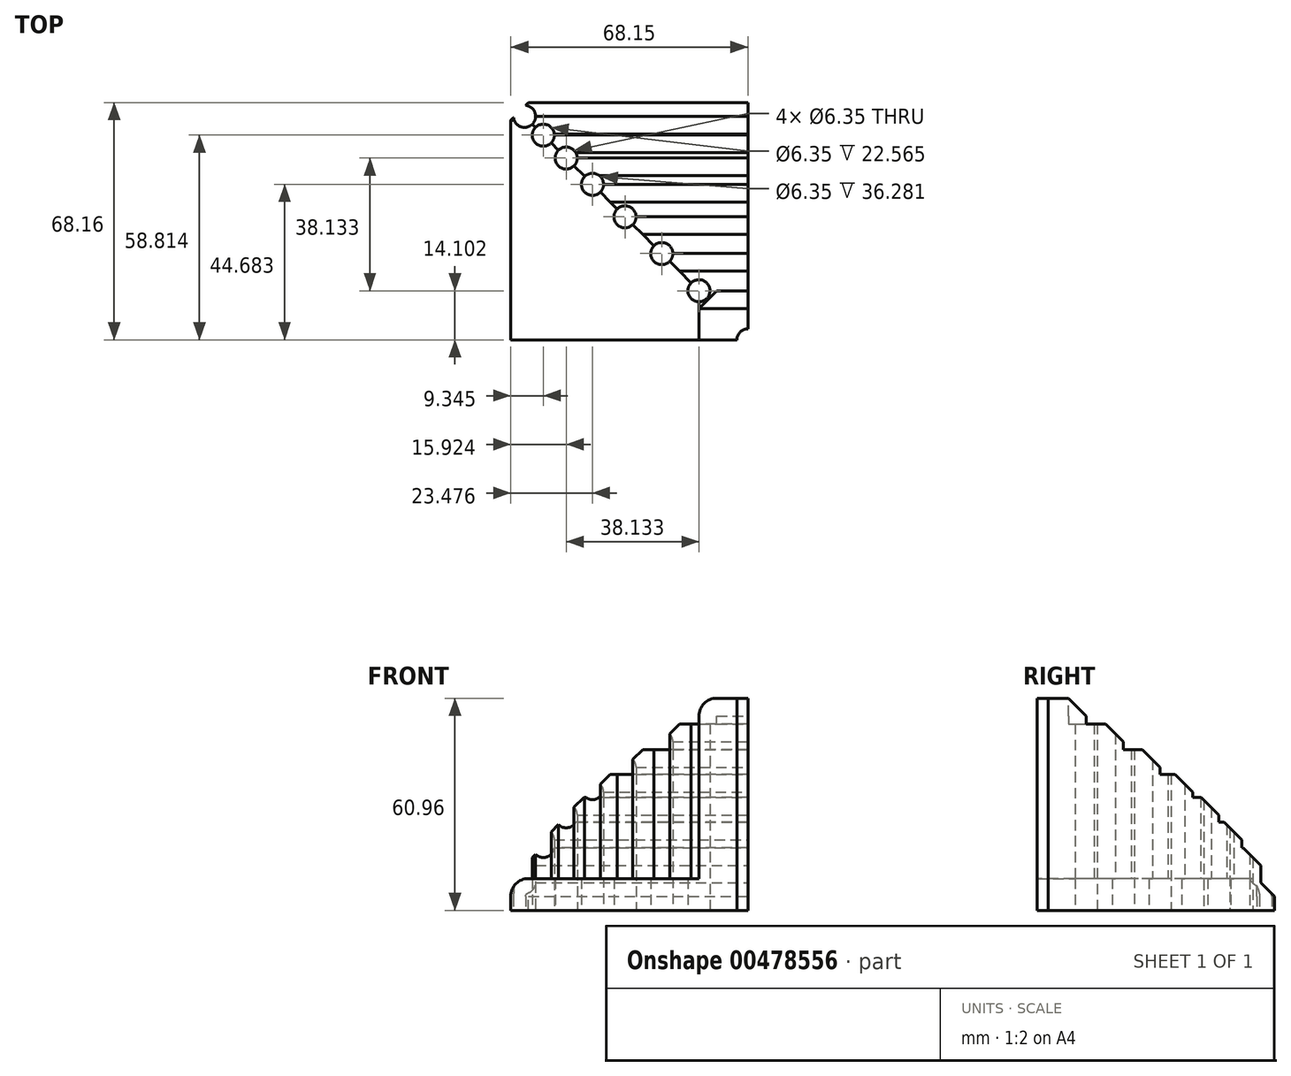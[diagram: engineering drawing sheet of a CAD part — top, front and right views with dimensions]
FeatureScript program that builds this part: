
annotation { "Feature Type Name" : "Feature", "Feature Type Description" : "" }
export const myFeature = defineFeature(function(context is Context, id is Id, definition is map)
    precondition{}
    {
        {
            var Q0;
            Q0=qCreatedBy(makeId("Top.planeOp"),FACE);
            var sketch = newSketch(context, id + "F0", { "sketchPlane" : qUnion([Q0])});
            skLineSegment(sketch, "E0.bottom", {"start": v(-29.57, 37.12) * mm, "end": v(38.58, 37.12) * mm});
            skLineSegment(sketch, "E0.top", {"start": v(-29.57, -31.04) * mm, "end": v(38.58, -31.04) * mm});
            skLineSegment(sketch, "E0.left", {"start": v(-29.57, 37.12) * mm, "end": v(-29.57, -31.04) * mm});
            skLineSegment(sketch, "E0.right", {"start": v(38.58, 37.12) * mm, "end": v(38.58, -31.04) * mm});
            skLineSegment(sketch, "E1.top", {"start": v(-27.22, -31.04) * mm, "end": v(38.58, -31.04) * mm});
            skLineSegment(sketch, "E1.right", {"start": v(38.58, 33.6) * mm, "end": v(38.58, -31.04) * mm});
            skLineSegment(sketch, "E2", {"start": v(-29.57, 37.12) * mm, "end": v(24.49, -16.94) * mm});
            skLineSegment(sketch, "E3.bottom", {"start": v(-25.63, 33.18) * mm, "end": v(38.58, 33.18) * mm});
            skLineSegment(sketch, "E3.top", {"start": v(-25.63, -31.04) * mm, "end": v(38.58, -31.04) * mm});
            skLineSegment(sketch, "E3.left", {"start": v(-25.63, 33.18) * mm, "end": v(-25.63, -31.04) * mm});
            skLineSegment(sketch, "E3.right", {"start": v(38.58, 33.18) * mm, "end": v(38.58, -31.04) * mm});
            skLineSegment(sketch, "E4.bottom", {"start": v(-20.22, 27.77) * mm, "end": v(38.58, 27.77) * mm});
            skLineSegment(sketch, "E4.top", {"start": v(-20.22, -31.04) * mm, "end": v(38.58, -31.04) * mm});
            skLineSegment(sketch, "E4.left", {"start": v(-20.22, 27.77) * mm, "end": v(-20.22, -31.04) * mm});
            skLineSegment(sketch, "E4.right", {"start": v(38.58, 27.77) * mm, "end": v(38.58, -31.04) * mm});
            skLineSegment(sketch, "E5.bottom", {"start": v(-13.65, 21.2) * mm, "end": v(38.58, 21.2) * mm});
            skLineSegment(sketch, "E5.top", {"start": v(-13.65, -31.04) * mm, "end": v(38.58, -31.04) * mm});
            skLineSegment(sketch, "E5.left", {"start": v(-13.65, 21.2) * mm, "end": v(-13.65, -31.04) * mm});
            skLineSegment(sketch, "E5.right", {"start": v(38.58, 21.2) * mm, "end": v(38.58, -31.04) * mm});
            skLineSegment(sketch, "E6.bottom", {"start": v(-6.1, 13.64) * mm, "end": v(38.58, 13.64) * mm});
            skLineSegment(sketch, "E6.top", {"start": v(-6.1, -31.04) * mm, "end": v(38.58, -31.04) * mm});
            skLineSegment(sketch, "E6.left", {"start": v(-6.1, 13.64) * mm, "end": v(-6.1, -31.04) * mm});
            skLineSegment(sketch, "E6.right", {"start": v(38.58, 13.64) * mm, "end": v(38.58, -31.04) * mm});
            skLineSegment(sketch, "E7.bottom", {"start": v(3.25, 4.3) * mm, "end": v(38.58, 4.3) * mm});
            skLineSegment(sketch, "E7.top", {"start": v(3.25, -31.04) * mm, "end": v(38.58, -31.04) * mm});
            skLineSegment(sketch, "E7.left", {"start": v(3.25, 4.3) * mm, "end": v(3.25, -31.04) * mm});
            skLineSegment(sketch, "E7.right", {"start": v(38.58, 4.3) * mm, "end": v(38.58, -31.04) * mm});
            skLineSegment(sketch, "E8.bottom", {"start": v(13.81, -6.26) * mm, "end": v(38.58, -6.26) * mm});
            skLineSegment(sketch, "E8.top", {"start": v(13.81, -31.04) * mm, "end": v(38.58, -31.04) * mm});
            skLineSegment(sketch, "E8.left", {"start": v(13.81, -6.26) * mm, "end": v(13.81, -31.04) * mm});
            skLineSegment(sketch, "E8.right", {"start": v(38.58, -6.26) * mm, "end": v(38.58, -31.04) * mm});
            skLineSegment(sketch, "E9.bottom", {"start": v(24.49, -16.94) * mm, "end": v(38.58, -16.94) * mm});
            skLineSegment(sketch, "E9.top", {"start": v(24.49, -31.04) * mm, "end": v(38.58, -31.04) * mm});
            skLineSegment(sketch, "E9.left", {"start": v(24.49, -16.94) * mm, "end": v(24.49, -31.04) * mm});
            skLineSegment(sketch, "E9.right", {"start": v(38.58, -16.94) * mm, "end": v(38.58, -31.04) * mm});
            skSolve(sketch);
        }
        {
            var Q0;
            {var subQ1=sQuery(id+"F0.wireOp",EDGE,"E0.bottom");Q0=makeQuery(id+"F0.imprint","IMPRINT",FACE,{"disambiguationData":[TD([[makeQuery(id+"F0.imprint","IMPRINT",EDGE,{"derivedFrom":subQ1}),-1.0]])]});}
            var Q1;
            Q1=makeQuery(id+"F0.imprint","IMPRINT",FACE,{"disambiguationData":[TD([[makeQuery(id+"F0.imprint","IMPRINT",EDGE,{"derivedFrom":sQuery(id+"F0.wireOp",EDGE,"E0.top")}),1.0]])]});
            extrude(context, id + "F1", {"entities" : qUnion([Q0, Q1]), "depth" : 9.14 * mm});
        }
        {
            var Q0;
            Q0=makeQuery(id+"F0.imprint","IMPRINT",FACE,{"disambiguationData":[TD([[makeQuery(id+"F0.imprint","IMPRINT",EDGE,{"derivedFrom":sQuery(id+"F0.wireOp",EDGE,"E3.top")}),1.0]])]});
            var Q1;
            {var subQ0=sQuery(id+"F0.wireOp",EDGE,"E3.bottom");Q1=makeQuery(id+"F0.imprint","IMPRINT",FACE,{"disambiguationData":[TD([[makeQuery(id+"F0.imprint","IMPRINT",EDGE,{"derivedFrom":subQ0}),-1.0]])]});}
            extrude(context, id + "F2", {"entities" : qUnion([Q0, Q1]), "operationType" : NewBodyOperationType.ADD, "depth" : 18.03 * mm});
        }
        {
            var Q0;
            Q0=makeQuery(id+"F0.imprint","IMPRINT",FACE,{"disambiguationData":[TD([[makeQuery(id+"F0.imprint","IMPRINT",EDGE,{"derivedFrom":sQuery(id+"F0.wireOp",EDGE,"E4.top")}),1.0]])]});
            var Q1;
            {var subQ0=sQuery(id+"F0.wireOp",EDGE,"E4.bottom");Q1=makeQuery(id+"F0.imprint","IMPRINT",FACE,{"disambiguationData":[TD([[makeQuery(id+"F0.imprint","IMPRINT",EDGE,{"derivedFrom":subQ0}),-1.0]])]});}
            extrude(context, id + "F3", {"entities" : qUnion([Q0, Q1]), "operationType" : NewBodyOperationType.ADD, "depth" : 25.4 * mm});
        }
        {
            var Q0;
            {var subQ0=sQuery(id+"F0.wireOp",EDGE,"E5.bottom");Q0=makeQuery(id+"F0.imprint","IMPRINT",FACE,{"disambiguationData":[TD([[makeQuery(id+"F0.imprint","IMPRINT",EDGE,{"derivedFrom":subQ0}),-1.0]])]});}
            var Q1;
            Q1=makeQuery(id+"F0.imprint","IMPRINT",FACE,{"disambiguationData":[TD([[makeQuery(id+"F0.imprint","IMPRINT",EDGE,{"derivedFrom":sQuery(id+"F0.wireOp",EDGE,"E5.top")}),1.0]])]});
            extrude(context, id + "F4", {"entities" : qUnion([Q0, Q1]), "operationType" : NewBodyOperationType.ADD, "depth" : 32.5 * mm});
        }
        {
            var Q0;
            Q0=makeQuery(id+"F0.imprint","IMPRINT",FACE,{"disambiguationData":[TD([[makeQuery(id+"F0.imprint","IMPRINT",EDGE,{"derivedFrom":sQuery(id+"F0.wireOp",EDGE,"E6.top")}),1.0]])]});
            var Q1;
            {var subQ0=sQuery(id+"F0.wireOp",EDGE,"E6.bottom");Q1=makeQuery(id+"F0.imprint","IMPRINT",FACE,{"disambiguationData":[TD([[makeQuery(id+"F0.imprint","IMPRINT",EDGE,{"derivedFrom":subQ0}),-1.0]])]});}
            extrude(context, id + "F5", {"entities" : qUnion([Q0, Q1]), "operationType" : NewBodyOperationType.ADD, "depth" : 39.12 * mm});
        }
        {
            var Q0;
            Q0=makeQuery(id+"F0.imprint","IMPRINT",FACE,{"disambiguationData":[TD([[makeQuery(id+"F0.imprint","IMPRINT",EDGE,{"derivedFrom":sQuery(id+"F0.wireOp",EDGE,"E7.top")}),1.0]])]});
            var Q1;
            {var subQ0=sQuery(id+"F0.wireOp",EDGE,"E7.bottom");Q1=makeQuery(id+"F0.imprint","IMPRINT",FACE,{"disambiguationData":[TD([[makeQuery(id+"F0.imprint","IMPRINT",EDGE,{"derivedFrom":subQ0}),-1.0]])]});}
            extrude(context, id + "F6", {"entities" : qUnion([Q0, Q1]), "operationType" : NewBodyOperationType.ADD, "depth" : 46.23 * mm});
        }
        {
            var Q0;
            {var subQ2=sQuery(id+"F0.wireOp",EDGE,"E8.bottom");Q0=makeQuery(id+"F0.imprint","IMPRINT",FACE,{"disambiguationData":[TD([[makeQuery(id+"F0.imprint","IMPRINT",EDGE,{"derivedFrom":subQ2}),-1.0]])]});}
            var Q1;
            Q1=makeQuery(id+"F0.imprint","IMPRINT",FACE,{"disambiguationData":[TD([[makeQuery(id+"F0.imprint","IMPRINT",EDGE,{"derivedFrom":sQuery(id+"F0.wireOp",EDGE,"E8.top")}),1.0]])]});
            extrude(context, id + "F7", {"entities" : qUnion([Q0, Q1]), "operationType" : NewBodyOperationType.ADD, "depth" : 53.6 * mm});
        }
        {
            var Q0;
            Q0=makeQuery(id+"F0.imprint","IMPRINT",FACE,{"disambiguationData":[TD([[makeQuery(id+"F0.imprint","IMPRINT",EDGE,{"derivedFrom":sQuery(id+"F0.wireOp",EDGE,"E9.bottom")}),-1.0]])]});
            extrude(context, id + "F8", {"entities" : qUnion([Q0]), "operationType" : NewBodyOperationType.ADD, "depth" : 60.96 * mm});
        }
        {
            var Q0;
            Q0=makeQuery(id+"F1.opExtrude","CAP_EDGE",EDGE,{"disambiguationData":[OSD([sQuery(id+"F0.wireOp",EDGE,"E0.left")])],"isStart":false});
            var Q1;
            Q1=makeQuery(id+"F2.opExtrude","CAP_EDGE",EDGE,{"disambiguationData":[OSD([sQuery(id+"F0.wireOp",EDGE,"E3.left")])],"isStart":false});
            var Q2;
            Q2=makeQuery(id+"F3.opExtrude","CAP_EDGE",EDGE,{"disambiguationData":[OSD([sQuery(id+"F0.wireOp",EDGE,"E4.left")])],"isStart":false});
            var Q3;
            Q3=makeQuery(id+"F4.opExtrude","CAP_EDGE",EDGE,{"disambiguationData":[OSD([sQuery(id+"F0.wireOp",EDGE,"E5.left")])],"isStart":false});
            var Q4;
            Q4=makeQuery(id+"F5.opExtrude","CAP_EDGE",EDGE,{"disambiguationData":[OSD([sQuery(id+"F0.wireOp",EDGE,"E6.left")])],"isStart":false});
            var Q5;
            Q5=makeQuery(id+"F6.opExtrude","CAP_EDGE",EDGE,{"disambiguationData":[OSD([sQuery(id+"F0.wireOp",EDGE,"E7.left")])],"isStart":false});
            var Q6;
            Q6=makeQuery(id+"F7.opExtrude","CAP_EDGE",EDGE,{"disambiguationData":[OSD([sQuery(id+"F0.wireOp",EDGE,"E8.left")])],"isStart":false});
            var Q7;
            Q7=makeQuery(id+"F8.opExtrude","CAP_EDGE",EDGE,{"disambiguationData":[OSD([sQuery(id+"F0.wireOp",EDGE,"E9.left")])],"isStart":false});
            fillet(context, id + "F9", {"entities" : qUnion([Q0, Q1, Q2, Q3, Q4, Q5, Q6, Q7]), "radius" : 5.08 * mm, "tangentPropagation" : true, "allowEdgeOverflow" : false});
        }
        {
            var Q0;
            Q0=makeQuery(id+"F3.opExtrude","CAP_EDGE",EDGE,{"disambiguationData":[OSD([sQuery(id+"F0.wireOp",EDGE,"E4.bottom")])],"isStart":false});
            var Q1;
            Q1=makeQuery(id+"F4.opExtrude","CAP_EDGE",EDGE,{"disambiguationData":[OSD([sQuery(id+"F0.wireOp",EDGE,"E5.bottom")])],"isStart":false});
            var Q2;
            Q2=makeQuery(id+"F5.opExtrude","CAP_EDGE",EDGE,{"disambiguationData":[OSD([sQuery(id+"F0.wireOp",EDGE,"E6.bottom")])],"isStart":false});
            var Q3;
            Q3=makeQuery(id+"F6.opExtrude","CAP_EDGE",EDGE,{"disambiguationData":[OSD([sQuery(id+"F0.wireOp",EDGE,"E7.bottom")])],"isStart":false});
            var Q4;
            Q4=makeQuery(id+"F7.opExtrude","CAP_EDGE",EDGE,{"disambiguationData":[OSD([sQuery(id+"F0.wireOp",EDGE,"E8.bottom")])],"isStart":false});
            var Q5;
            Q5=makeQuery(id+"F8.opExtrude","CAP_EDGE",EDGE,{"disambiguationData":[OSD([sQuery(id+"F0.wireOp",EDGE,"E9.bottom")])],"isStart":false});
            var Q6;
            Q6=makeQuery(id+"F2.opExtrude","CAP_EDGE",EDGE,{"disambiguationData":[OSD([sQuery(id+"F0.wireOp",EDGE,"E3.bottom")])],"isStart":false});
            chamfer(context, id + "F10", {"entities" : qUnion([Q0, Q1, Q2, Q3, Q4, Q5, Q6]), "width" : 5.08 * mm, "tangentPropagation" : true});
        }
        {
            var Q0;
            Q0=makeQuery(id+"F1.opExtrude","CAP_EDGE",EDGE,{"disambiguationData":[OSD([sQuery(id+"F0.wireOp",EDGE,"E0.bottom")])],"isStart":false});
            chamfer(context, id + "F11", {"entities" : qUnion([Q0]), "width" : 5.08 * mm, "tangentPropagation" : true});
        }
        {
            var Q0;
            Q0=sQuery(id+"F0.wireOp",VERTEX,"E0.bottom.start");
            var Q1;
            Q1=sQuery(id+"F0.wireOp",VERTEX,"E7.left.start");
            var Q2;
            Q2=sQuery(id+"F0.wireOp",VERTEX,"E5.left.start");
            var Q3;
            Q3=sQuery(id+"F0.wireOp",VERTEX,"E3.left.start");
            var Q4;
            Q4=sQuery(id+"F0.wireOp",VERTEX,"E4.bottom.start");
            var Q5;
            Q5=sQuery(id+"F0.wireOp",VERTEX,"E6.bottom.start");
            var Q6;
            Q6=sQuery(id+"F0.wireOp",VERTEX,"E9.left.start");
            var Q7;
            Q7=sQuery(id+"F0.wireOp",VERTEX,"E8.bottom.start");
            var Q8;
            Q8=sQuery(id+"F0.wireOp",VERTEX,"E8.top.end");
            var Q9;
            Q9=makeQuery(id+"F1.opExtrude","SWEPT_BODY",BODY,{"disambiguationData":[OSD([sQuery(id+"F0.wireOp",EDGE,"E0.bottom"),sQuery(id+"F0.wireOp",EDGE,"E0.top"),sQuery(id+"F0.wireOp",EDGE,"E0.left"),sQuery(id+"F0.wireOp",EDGE,"E0.right"),sQuery(id+"F0.wireOp",EDGE,"E1.top"),sQuery(id+"F0.wireOp",EDGE,"E1.right"),sQuery(id+"F0.wireOp",EDGE,"E3.bottom"),sQuery(id+"F0.wireOp",EDGE,"E3.left")])]});
            hole(context, id + "F12", {"style" : HoleStyle.SIMPLE, "endStyle" : HoleEndStyle.THROUGH, "oppositeDirection" : true, "holeDiameter" : 6.35 * mm, "isTappedThrough" : true, "tappedDepth" : 12.7 * mm, "tapClearance" : 3, "locations" : qUnion([Q0, Q1, Q2, Q3, Q4, Q5, Q6, Q7, Q8]), "scope" : qUnion([Q9])});
        }
    });
